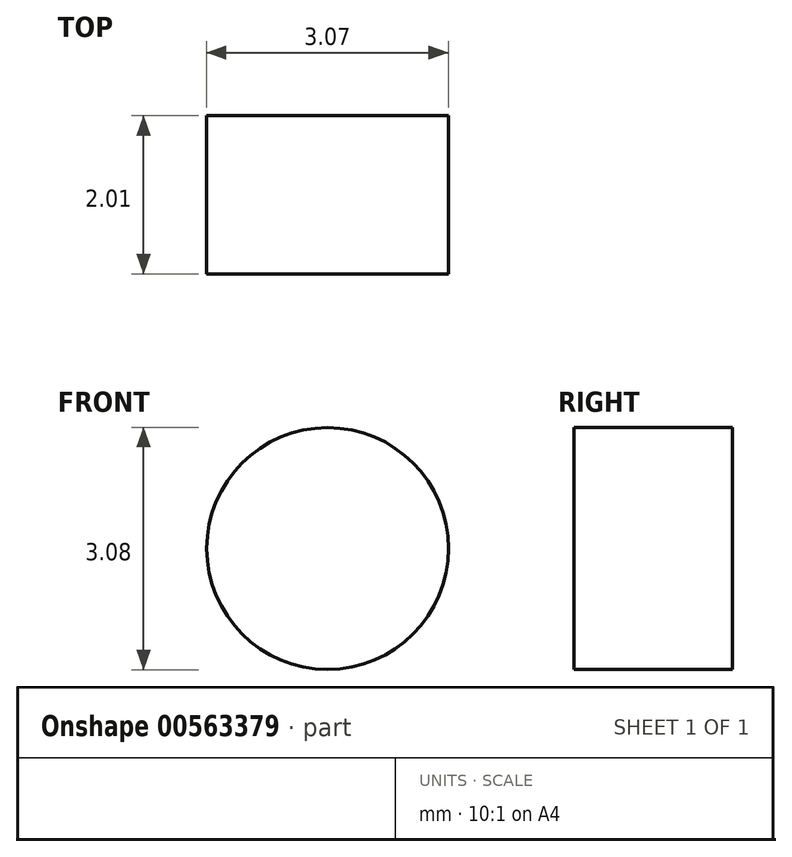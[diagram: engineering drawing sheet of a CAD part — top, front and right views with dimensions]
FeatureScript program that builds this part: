
annotation { "Feature Type Name" : "Feature", "Feature Type Description" : "" }
export const myFeature = defineFeature(function(context is Context, id is Id, definition is map)
    precondition{}
    {
        {
            var Q0;
            Q0=qCreatedBy(makeId("Front.planeOp"),FACE);
            var sketch = newSketch(context, id + "F0", { "sketchPlane" : qUnion([Q0])});
            skCircle(sketch, "E0", {"center": v(-16.97, 9.84) * mm, "radius": 1.54 * mm});
            skSolve(sketch);
        }
        {
            var Q0;
            Q0=qSketchRegion(id+"F0",true);
            extrude(context, id + "F1", {"entities" : qUnion([Q0]), "depth" : 2 * mm});
        }
    });
